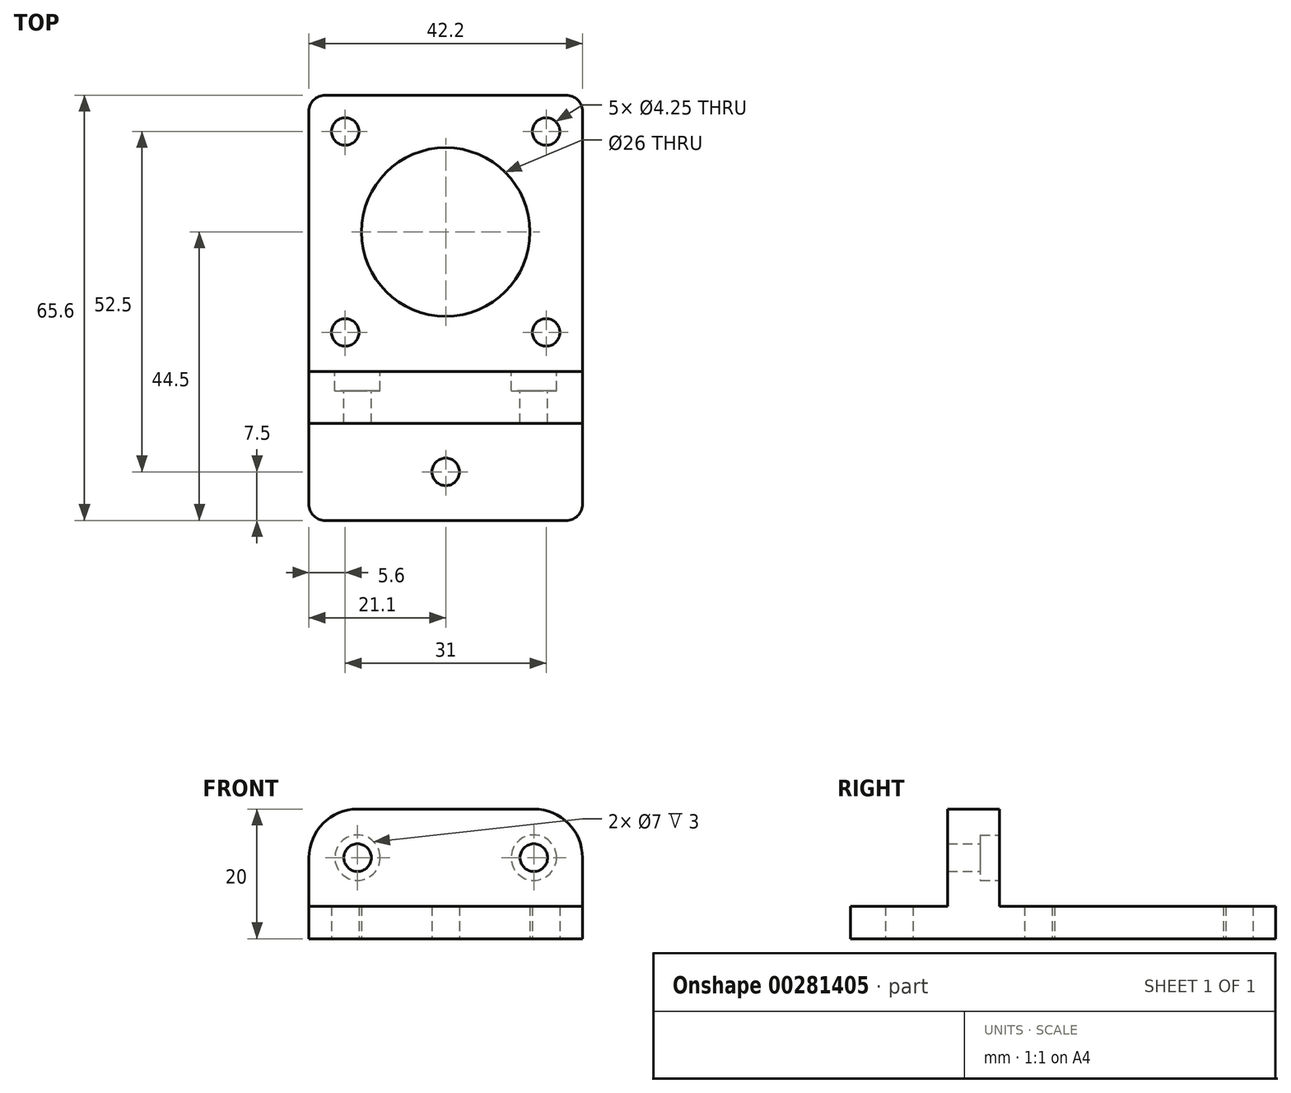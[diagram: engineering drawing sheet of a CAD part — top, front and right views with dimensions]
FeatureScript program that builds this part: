
annotation { "Feature Type Name" : "Feature", "Feature Type Description" : "" }
export const myFeature = defineFeature(function(context is Context, id is Id, definition is map)
    precondition{}
    {
        {
            var Q0;
            Q0=qCreatedBy(makeId("Top.planeOp"),FACE);
            var sketch = newSketch(context, id + "F0", { "sketchPlane" : qUnion([Q0])});
            skLineSegment(sketch, "E0.bottom", {"start": v(15.5, -15.5) * mm, "end": v(-15.5, -15.5) * mm, "construction": true});
            skLineSegment(sketch, "E0.top", {"start": v(15.5, 15.5) * mm, "end": v(-15.5, 15.5) * mm, "construction": true});
            skLineSegment(sketch, "E0.left", {"start": v(15.5, -15.5) * mm, "end": v(15.5, 15.5) * mm, "construction": true});
            skLineSegment(sketch, "E0.right", {"start": v(-15.5, -15.5) * mm, "end": v(-15.5, 15.5) * mm, "construction": true});
            skPoint(sketch, "E0.middle", {"position": v(0, 0) * mm});
            skCircle(sketch, "E1", {"center": v(0, 0) * mm, "radius": 13 * mm});
            skCircle(sketch, "E2", {"center": v(-15.5, 15.5) * mm, "radius": 2.12 * mm});
            skCircle(sketch, "E3", {"center": v(15.5, 15.5) * mm, "radius": 2.12 * mm});
            skCircle(sketch, "E4", {"center": v(15.5, -15.5) * mm, "radius": 2.12 * mm});
            skCircle(sketch, "E5", {"center": v(-15.5, -15.5) * mm, "radius": 2.12 * mm});
            skLineSegment(sketch, "E6", {"start": v(-18.6, 21.1) * mm, "end": v(18.6, 21.1) * mm});
            skLineSegment(sketch, "E7", {"start": v(21.1, 18.6) * mm, "end": v(21.1, -42) * mm});
            skLineSegment(sketch, "E8", {"start": v(18.6, -44.5) * mm, "end": v(-18.6, -44.5) * mm});
            skLineSegment(sketch, "E9", {"start": v(-21.1, -42) * mm, "end": v(-21.1, 18.6) * mm});
            skCircle(sketch, "E10", {"center": v(0, -37) * mm, "radius": 2.12 * mm});
            skPoint(sketch, "E11.visualSharp", {"position": v(-21.1, -44.5) * mm});
            skArc(sketch, "E11.filletArc", {"start": v(-21.1, -42) * mm, "mid": v(-20.37, -43.77) * mm, "end": v(-18.6, -44.5) * mm});
            skPoint(sketch, "E12.visualSharp", {"position": v(21.1, -44.5) * mm});
            skArc(sketch, "E12.filletArc", {"start": v(18.6, -44.5) * mm, "mid": v(20.37, -43.77) * mm, "end": v(21.1, -42) * mm});
            skPoint(sketch, "E13.visualSharp", {"position": v(21.1, 21.1) * mm});
            skArc(sketch, "E13.filletArc", {"start": v(21.1, 18.6) * mm, "mid": v(20.37, 20.37) * mm, "end": v(18.6, 21.1) * mm});
            skPoint(sketch, "E14.visualSharp", {"position": v(-21.1, 21.1) * mm});
            skArc(sketch, "E14.filletArc", {"start": v(-18.6, 21.1) * mm, "mid": v(-20.37, 20.37) * mm, "end": v(-21.1, 18.6) * mm});
            skSolve(sketch);
        }
        {
            var Q0;
            Q0=qSketchRegion(id+"F0",true);
            extrude(context, id + "F1", {"entities" : qUnion([Q0]), "depth" : 5 * mm});
        }
        {
            var Q0;
            Q0=makeQuery(id+"F1.opExtrude","CAP_FACE",FACE,{"disambiguationData":[OSD([sQuery(id+"F0.wireOp",EDGE,"E1"),sQuery(id+"F0.wireOp",EDGE,"E2"),sQuery(id+"F0.wireOp",EDGE,"E3"),sQuery(id+"F0.wireOp",EDGE,"E4"),sQuery(id+"F0.wireOp",EDGE,"E5"),sQuery(id+"F0.wireOp",EDGE,"E6"),sQuery(id+"F0.wireOp",EDGE,"E7"),sQuery(id+"F0.wireOp",EDGE,"E8"),sQuery(id+"F0.wireOp",EDGE,"E9"),sQuery(id+"F0.wireOp",EDGE,"E10"),sQuery(id+"F0.wireOp",EDGE,"E11.filletArc"),sQuery(id+"F0.wireOp",EDGE,"E12.filletArc"),sQuery(id+"F0.wireOp",EDGE,"E13.filletArc"),sQuery(id+"F0.wireOp",EDGE,"E14.filletArc")])],"isStart":false});
            var sketch = newSketch(context, id + "F2", { "sketchPlane" : qUnion([Q0])});
            skLineSegment(sketch, "E15.bottom", {"start": v(21.1, -29.5) * mm, "end": v(-21.1, -29.5) * mm});
            skLineSegment(sketch, "E15.top", {"start": v(21.1, -21.5) * mm, "end": v(-21.1, -21.5) * mm});
            skLineSegment(sketch, "E15.left", {"start": v(21.1, -29.5) * mm, "end": v(21.1, -21.5) * mm});
            skLineSegment(sketch, "E15.right", {"start": v(-21.1, -29.5) * mm, "end": v(-21.1, -21.5) * mm});
            skPoint(sketch, "E15.middle", {"position": v(0, -25.5) * mm});
            skSolve(sketch);
        }
        {
            var Q0;
            Q0=qSketchRegion(id+"F2",true);
            extrude(context, id + "F3", {"entities" : qUnion([Q0]), "operationType" : NewBodyOperationType.ADD, "depth" : 15 * mm});
        }
        {
            var Q0;
            Q0=makeQuery(id+"F3.opExtrude","CAP_EDGE",EDGE,{"disambiguationData":[OSD([sQuery(id+"F2.wireOp",EDGE,"E15.right")])],"isStart":false});
            var Q1;
            Q1=makeQuery(id+"F3.opExtrude","CAP_EDGE",EDGE,{"disambiguationData":[OSD([sQuery(id+"F2.wireOp",EDGE,"E15.left")])],"isStart":false});
            fillet(context, id + "F4", {"entities" : qUnion([Q0, Q1]), "radius" : 7.5 * mm, "tangentPropagation" : true, "allowEdgeOverflow" : false});
        }
        {
            var Q0;
            Q0=makeQuery(id+"F3.opExtrude","SWEPT_FACE",FACE,{"disambiguationData":[OSD([sQuery(id+"F2.wireOp",EDGE,"E15.top")])]});
            var sketch = newSketch(context, id + "F5", { "sketchPlane" : qUnion([Q0])});
            skCircle(sketch, "E16", {"center": v(-13.6, 12.5) * mm, "radius": 2.12 * mm});
            skCircle(sketch, "E17", {"center": v(13.6, 12.5) * mm, "radius": 2.12 * mm});
            skSolve(sketch);
        }
        {
            var Q0;
            Q0=qSketchRegion(id+"F5",true);
            extrude(context, id + "F6", {"entities" : qUnion([Q0]), "operationType" : NewBodyOperationType.REMOVE, "endBound" : BoundingType.THROUGH_ALL, "oppositeDirection" : true, "depth" : 25 * mm});
        }
        {
            var Q0;
            Q0=makeQuery(id+"F3.opExtrude","SWEPT_FACE",FACE,{"disambiguationData":[OSD([sQuery(id+"F2.wireOp",EDGE,"E15.top")])]});
            var sketch = newSketch(context, id + "F7", { "sketchPlane" : qUnion([Q0])});
            skCircle(sketch, "E18", {"center": v(-13.6, 12.5) * mm, "radius": 3.5 * mm});
            skCircle(sketch, "E19", {"center": v(13.6, 12.5) * mm, "radius": 3.5 * mm});
            skSolve(sketch);
        }
        {
            var Q0;
            Q0=qSketchRegion(id+"F7",true);
            extrude(context, id + "F8", {"entities" : qUnion([Q0]), "operationType" : NewBodyOperationType.REMOVE, "oppositeDirection" : true, "depth" : 3 * mm});
        }
    });
